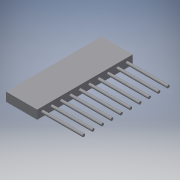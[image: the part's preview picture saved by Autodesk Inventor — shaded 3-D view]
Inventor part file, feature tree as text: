
AUTODESK INVENTOR PART (.ipt)
format: ipt  version: 2019.4 (Build 234330000, 330)  size: 133,120 bytes
history: native  units: mm
features: extrude x3, sketch x3, pattern_linear x1, projected_geometry x1
ambient origin geometry x8: Origin, YZ Plane, XZ Plane, XY Plane, X Axis, Y Axis, Z Axis, Center Point
bodies: Solid1 (feature_tree)
feature tree (8):
  extrude  "Extrusion1"  Depth=25.84mm
  extrude  "Extrusion2"  Depth=8.43mm
  extrude  "Extrusion3"  Depth=11.15mm TaperAngle=0.0deg
  pattern_linear  "Rectangular Pattern1"  Count1=10 Spacing1=2.54mm
  sketch  "Sketch1"  dims[d0=2.37mm d1=25.84mm]
  sketch  "Sketch2"  dims[d2=8.43mm d3=0.0mm d4=0.75mm]
  projected_geometry  "Projected Loop1"
  sketch  "Sketch3"  dims[d5=1.45mm d6=11.15mm d7=0.0mm d8=100.0mm d10=2.54mm d11=7.0mm d12=0.0mm]
